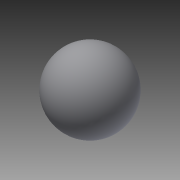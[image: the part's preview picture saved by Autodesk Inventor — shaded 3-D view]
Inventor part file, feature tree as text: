
AUTODESK INVENTOR PART (.ipt)
format: ipt  version: 2014 (Build 180170000, 170)  size: 101,376 bytes
history: native  units: in
note: dims shown in document units (in); Inventor stores cm internally (conversion verified against a paired STEP export)
features: plane x4, revolve x1, sketch x1
ambient origin geometry x8: Origin, YZ Plane, XZ Plane, XY Plane, X Axis, Y Axis, Z Axis, Center Point
bodies: Solid1 (feature_tree)
feature tree (6):
  revolve  "Revolution1"  Angle=90.0deg
  plane  "Work Plane2"
  plane  "Work Plane3"
  plane  "Work Plane5"
  sketch  "Sketch1"  dims[d0=10.0in d1=90.0deg d2=5.0in d3=-10.0in d4=5.0in d6=-5.0in]
  plane  "Work Plane1"
